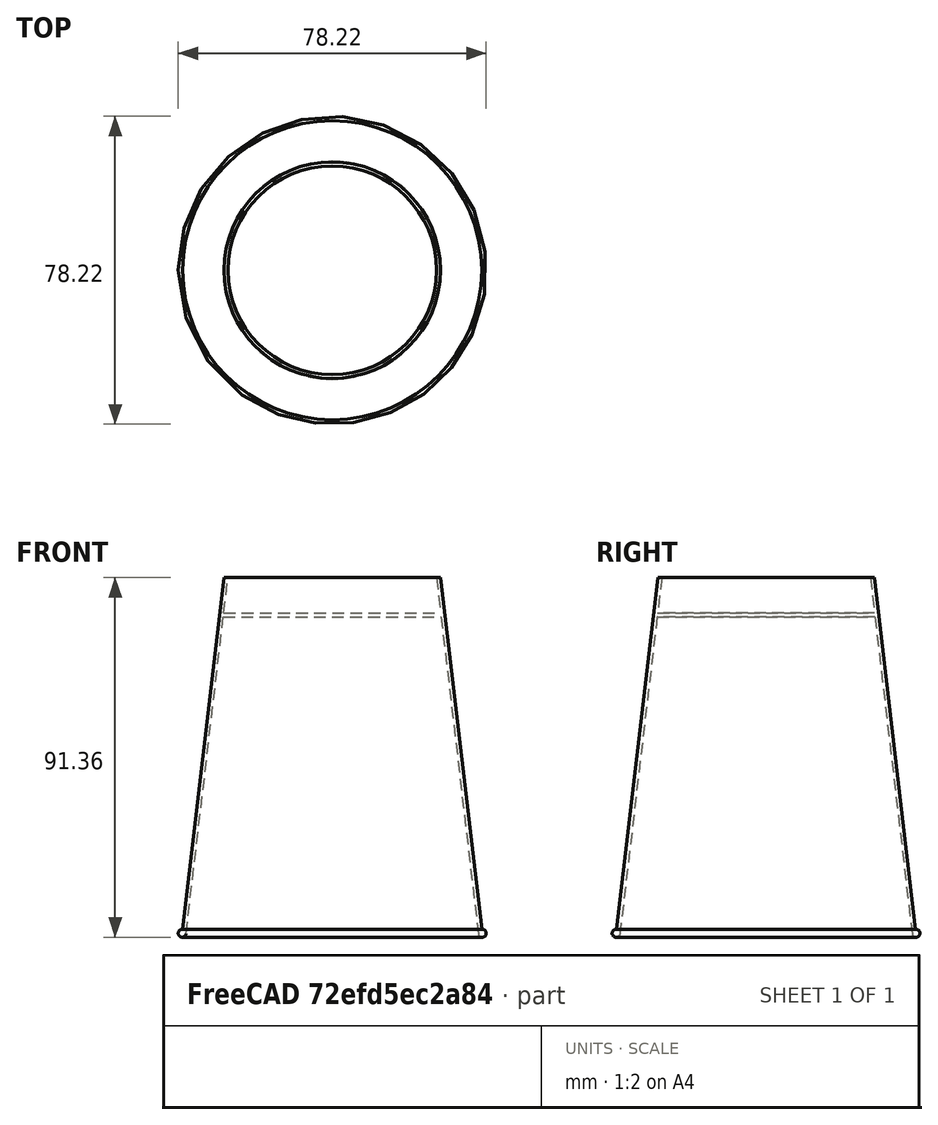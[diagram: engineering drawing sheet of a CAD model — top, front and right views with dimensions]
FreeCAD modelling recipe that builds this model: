
FCSTD DOCUMENT  (FreeCAD 0.21R33694 (Git))
Label: vibro_monster_v1
License: CERN Open Hardware Licence permissive
LicenseURL: https://cern-ohl.web.cern.ch/
objects: Sketcher::SketchObject×1, PartDesign::Revolution×1, PartDesign::Body×1
note: 4 computed .brp shape members not serialized (recipe doc carries the construction recipe); baked Part::Feature solids carry a one-line shape summary decoded from their .brp

FEATURE [Sketcher::SketchObject] Sketch
  FullyConstrained = true
  MapMode = 5
  Placement = pos=(0,0,0) rot=(1,0,0;1.5708rad)
  Support = -> [XZ_Plane]
  sketch-geometry (9):
    g0: LineSegment StartX=0 StartY=82.365 StartZ=0 EndX=-27.5572 EndY=82.365 EndZ=0
    g1: LineSegment StartX=-27.5572 StartY=82.365 StartZ=0 EndX=-26.5 EndY=91.365 EndZ=0
    g2: LineSegment StartX=-26.5 StartY=91.365 StartZ=0 EndX=-27.5 EndY=91.365 EndZ=0
    g3: LineSegment StartX=-27.5 StartY=91.365 StartZ=0 EndX=-38 EndY=1.97956 EndZ=0
    g4: LineSegment StartX=-37.1295 StartY=0.877301 StartZ=0 EndX=-27.6747 EndY=81.365 EndZ=0
    g5: LineSegment StartX=-27.6747 StartY=81.365 StartZ=0 EndX=0 EndY=81.365 EndZ=0
    g6: LineSegment StartX=0 StartY=81.365 StartZ=0 EndX=0 EndY=82.365 EndZ=0
    g7: LineSegment StartX=-27.5572 StartY=82.365 StartZ=0 EndX=-27.6747 EndY=81.365 EndZ=0
    g8: ArcOfCircle CenterX=-38.1159 CenterY=0.993171 CenterZ=0 NormalX=0 NormalY=0 NormalZ=1 AngleXU=0 Radius=0.993171 StartAngle=1.45386 EndAngle=6.16625
  constraints (26):
    c: PointOnObject(g0,g-2)
    c: Horizontal(g0)
    c: Coincident(g0,g1)
    c: Coincident(g1,g2)
    c: Horizontal(g2)
    c: Coincident(g4,g5)
    c: Horizontal(g5)
    c: Coincident(g5,g6)
    c: Coincident(g6,g0)
    c: Vertical(g6)
    c: DistanceX(g2) = -27.5
    c: DistanceX(g2,g2) = 1
    c: Parallel(g3,g1)
    c: Parallel(g4,g3)
    c: Coincident(g7,g0)
    c: Coincident(g7,g4)
    c: Parallel(g7,g1)
    c: Distance(g1,g0) = 9
    c: DistanceY(g6,g6) = 1
    c: Coincident(g2,g3)
    c: Coincident(g8,g3)
    c: Tangent(g8,g-1)
    c: Tangent(g8,g4) = -1.5708
    c: Perpendicular(g8,g3)
    c: Distance(g3) = 90
    c: DistanceX(g3,g-1) = 38
FEATURE [PartDesign::Revolution] Revolution
  Angle = 360
  Axis = (0,2e-16,1)
  Base = (0,0,0)
  Placement = pos=(0,0,0) rot=(1,0,0;1.5708rad)
  Profile = -> Sketch
  ReferenceAxis = -> Sketch [V_Axis]
FEATURE [PartDesign::Body] Body
  Group = -> [Sketch,Revolution]
  Origin = -> Origin
  Tip = -> Revolution
